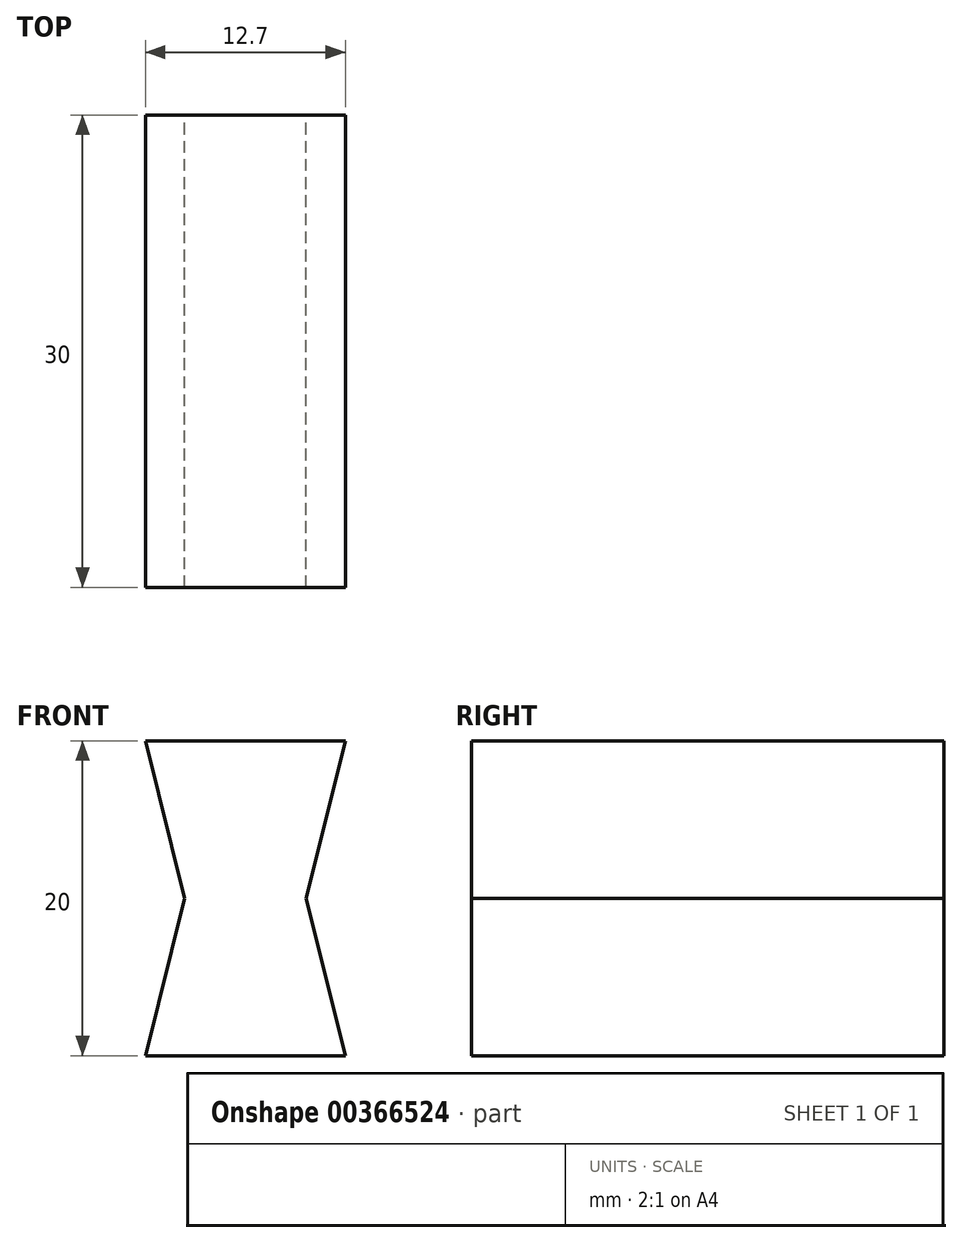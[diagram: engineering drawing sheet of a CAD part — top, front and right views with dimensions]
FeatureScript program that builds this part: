
annotation { "Feature Type Name" : "Feature", "Feature Type Description" : "" }
export const myFeature = defineFeature(function(context is Context, id is Id, definition is map)
    precondition{}
    {
        {
            var Q0;
            Q0=qCreatedBy(makeId("Front.planeOp"),FACE);
            var sketch = newSketch(context, id + "F0", { "sketchPlane" : qUnion([Q0])});
            skLineSegment(sketch, "E0.bottom", {"start": v(-7.56, 0) * mm, "end": v(13.59, 0) * mm});
            skLineSegment(sketch, "E0.top", {"start": v(-7.56, 18) * mm, "end": v(42.44, 18) * mm});
            skLineSegment(sketch, "E0.left", {"start": v(-7.56, 0) * mm, "end": v(-7.56, 18) * mm});
            skLineSegment(sketch, "E0.right", {"start": v(42.44, 0) * mm, "end": v(42.44, 18) * mm});
            skLineSegment(sketch, "E1.0", {"start": v(11.1, 10) * mm, "end": v(23.8, 10) * mm});
            skLineSegment(sketch, "E2", {"start": v(11.1, 10) * mm, "end": v(13.59, 0) * mm});
            skLineSegment(sketch, "E3", {"start": v(23.8, 10) * mm, "end": v(21.3, 0) * mm});
            skPoint(sketch, "E4.orphan", {"position": v(17.44, 18) * mm});
            skLineSegment(sketch, "E5.trimOffspring", {"start": v(21.3, 0) * mm, "end": v(42.44, 0) * mm});
            skPoint(sketch, "E6.start.orphan", {"position": v(17.44, 0) * mm});
            skLineSegment(sketch, "E7.MirrorCS", {"start": v(11.1, -10) * mm, "end": v(13.59, 0) * mm});
            skLineSegment(sketch, "E8.MirrorCS", {"start": v(11.1, -10) * mm, "end": v(23.8, -10) * mm});
            skLineSegment(sketch, "E9.MirrorCS", {"start": v(23.8, -10) * mm, "end": v(21.3, 0) * mm});
            skSolve(sketch);
        }
        {
            var Q0;
            Q0=makeQuery(id+"F0.imprint","IMPRINT",FACE,{"disambiguationData":[TD([[makeQuery(id+"F0.imprint","IMPRINT",EDGE,{"derivedFrom":sQuery(id+"F0.wireOp",EDGE,"E1.0")}),-1.0]])]});
            extrude(context, id + "F1", {"entities" : qUnion([Q0]), "depth" : 30 * mm});
        }
    });
